# Revit family: Light_Fixture-Wall_Sconce-KOHLER-MARGAUX-K-16268T
name_source: partatom
category: Lighting Fixtures
revit_build: Autodesk Revit 2017 (Build: 20160225_1515(x64)
units: mm (PartAtom-declared; Revit-internal decimal feet)

## family parameters
Cut with Voids When Loaded = No
Host = Face
Light Source = Yes
OmniClass Number = 23.35.47.11
OmniClass Title = Lighting Fixtures
Part Type = Normal
Room Calculation Point = No
Round Connector Dimension = Use Diameter
Shared = No

## types (2) — shared parameters
ADA Compliant = No
Apparent Load = 0 VA
Assembly Code = D5040.50
Color Filter = 16777215
Date Modified = 04/13/2021
Default Elevation = 48"
Description = Wall Lamp (1 head)
Dimming Lamp Color Temperature Shift = <None>
Electrical Connector = Yes
Electrical Note = One Dedicated Circuit Requiered
Emit from Line Length = 2"
Hardware Included = No
Height = 11 13/16"
Lamp = E14
Length = 5 11/16"
Light Source Symbol Size = 2"
Manufacturer = KOHLER Co.
Master Format 2014 = 26 51 13
Master Format 2014 Name = Interior Lighting Fixtures, Lamps, And Ballasts
Material = Premium Metal Construction
Product Documentation Link = https://files.kohler.com.cn
Product Name = MARGAUX
Product Page URL = https://www.kohler.com.cn
URL = http://www.kohler.com.cn
Voltage = 0 V
WaterSense Certified = No
Width = 4 7/8"

## per-type parameters (varying)
| type | Finish | Model | Type |
| CP-Polished Chrome | Kohler-Metal-CP-Polished_Chrome | K-16268T-CP | 1 |
| AF-Flange Gold | Kohler-Metal-AF-Flange_Gold | K-16268T-AF | 2 |

## geometry (parser evidence)
native form markers: Sweep x6
no freeform markers — native parametric forms only
